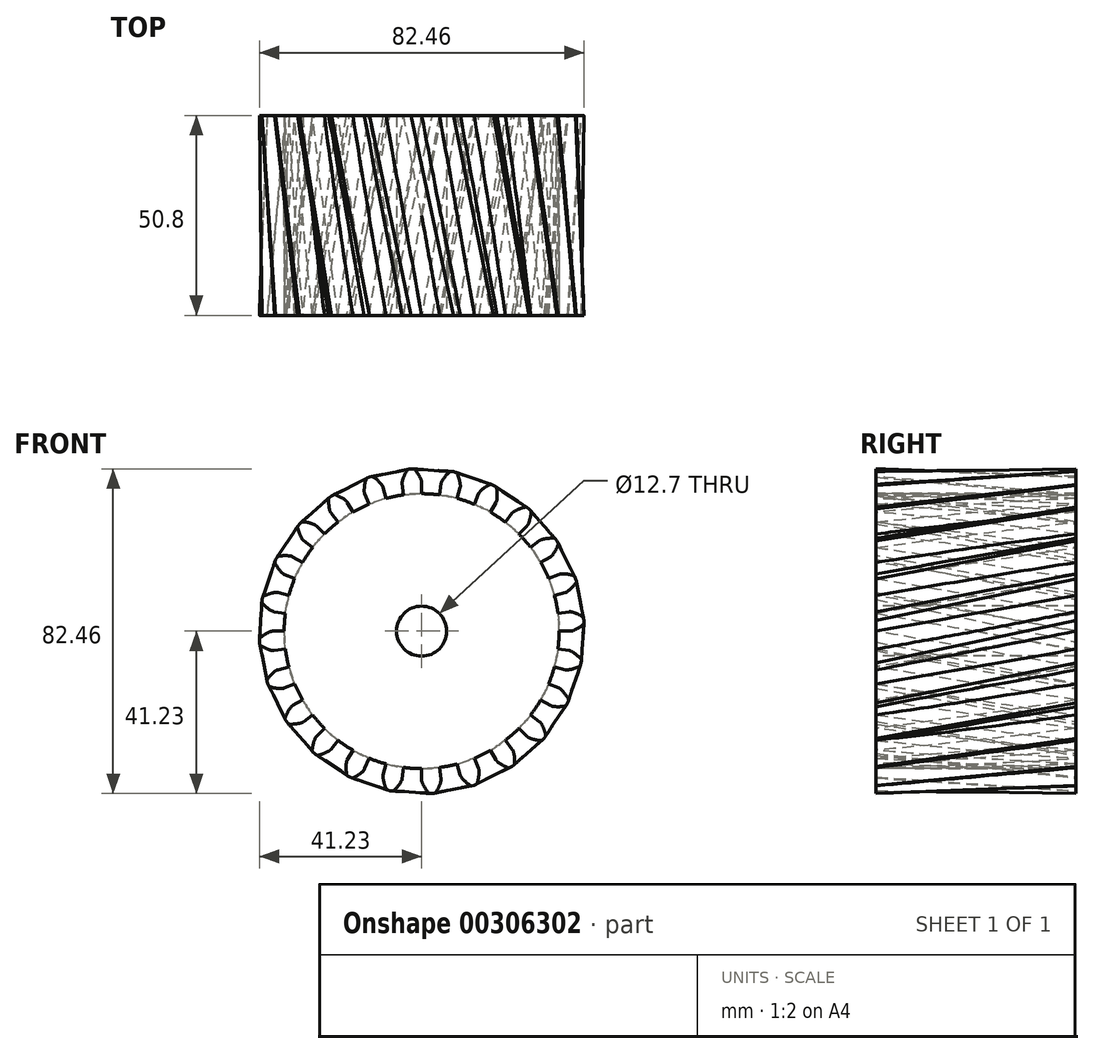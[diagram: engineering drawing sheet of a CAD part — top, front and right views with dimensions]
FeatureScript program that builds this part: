
annotation { "Feature Type Name" : "Feature", "Feature Type Description" : "" }
export const myFeature = defineFeature(function(context is Context, id is Id, definition is map)
    precondition{}
    {
        {
            var Q0;
            Q0=qCreatedBy(makeId("Front.planeOp"),FACE);
            var sketch = newSketch(context, id + "F0", { "sketchPlane" : qUnion([Q0])});
            skCircle(sketch, "E0", {"center": v(0, 0) * mm, "radius": 34.93 * mm});
            skArc(sketch, "E1.trimOffspring", {"start": v(-0.11, 38.4) * mm, "mid": v(-0.81, 39.8) * mm, "end": v(-1.73, 41.06) * mm});
            skLineSegment(sketch, "E2", {"start": v(0, 37.8) * mm, "end": v(0, 34.93) * mm});
            skLineSegment(sketch, "E3", {"start": v(-2.12, 41.23) * mm, "end": v(-2.7, 41.23) * mm});
            skArc(sketch, "E4.MirrorCS", {"start": v(-4.9, 38.09) * mm, "mid": v(-4.39, 39.56) * mm, "end": v(-3.64, 40.93) * mm});
            skLineSegment(sketch, "E5.MirrorCS", {"start": v(-4.93, 37.48) * mm, "end": v(-4.56, 34.63) * mm});
            skLineSegment(sketch, "E6.MirrorCS", {"start": v(-3.28, 41.16) * mm, "end": v(-2.7, 41.23) * mm});
            skPoint(sketch, "E7.visualSharp", {"position": v(-3.51, 41.13) * mm});
            skArc(sketch, "E7.filletArc", {"start": v(-3.28, 41.16) * mm, "mid": v(-3.49, 41.08) * mm, "end": v(-3.64, 40.93) * mm});
            skPoint(sketch, "E8.visualSharp", {"position": v(-1.89, 41.23) * mm});
            skArc(sketch, "E8.filletArc", {"start": v(-1.73, 41.06) * mm, "mid": v(-1.9, 41.19) * mm, "end": v(-2.12, 41.23) * mm});
            skPoint(sketch, "E9.visualSharp", {"position": v(0, 38.1) * mm});
            skArc(sketch, "E9.filletArc", {"start": v(0, 37.8) * mm, "mid": v(-0.03, 38.1) * mm, "end": v(-0.11, 38.4) * mm});
            skPoint(sketch, "E10.visualSharp", {"position": v(-4.97, 37.77) * mm});
            skArc(sketch, "E10.filletArc", {"start": v(-4.9, 38.09) * mm, "mid": v(-4.95, 37.79) * mm, "end": v(-4.93, 37.48) * mm});
            skSolve(sketch);
        }
        {
            var Q0;
            {var subQ0=sQuery(id+"F0.wireOp",EDGE,"E0");var subQ1=makeQuery(id+"F0.imprint","INTERSECT",VERTEX,{"derivedFrom":[subQ0,sQuery(id+"F0.wireOp",EDGE,"E2")]});Q0=makeQuery(id+"F0.imprint","IMPRINT",FACE,{"disambiguationData":[TD([[makeQuery(id+"F0.imprint","IMPRINT",EDGE,{"disambiguationData":[TD([[subQ1,-1.0]])],"derivedFrom":subQ0}),1.0]])]});}
            cPlane(context, id + "F1", {"entities" : qUnion([Q0]), "cplaneType" : CPlaneType.OFFSET, "offset" : 50.8 * mm, "width" : 152.4 * mm, "height" : 152.4 * mm});
        }
        {
            var Q0;
            Q0=qCreatedBy(id+"F1.planeOp",FACE);
            var sketch = newSketch(context, id + "F2", { "sketchPlane" : qUnion([Q0])});
            skCircle(sketch, "E11.0", {"center": v(0, 0) * mm, "radius": 34.93 * mm});
            skArc(sketch, "E12.0.0", {"start": v(-3.64, 40.93) * mm, "mid": v(-4.39, 39.56) * mm, "end": v(-4.9, 38.09) * mm});
            skArc(sketch, "E12.0.1", {"start": v(-4.9, 38.09) * mm, "mid": v(-4.95, 37.79) * mm, "end": v(-4.93, 37.48) * mm});
            skLineSegment(sketch, "E12.0.2", {"start": v(-4.93, 37.48) * mm, "end": v(-4.56, 34.63) * mm});
            skArc(sketch, "E12.0.3", {"start": v(-4.56, 34.63) * mm, "mid": v(-2.28, 34.85) * mm, "end": v(0, 34.92) * mm});
            skLineSegment(sketch, "E12.0.4", {"start": v(0, 34.93) * mm, "end": v(0, 37.8) * mm});
            skArc(sketch, "E12.0.5", {"start": v(0, 37.8) * mm, "mid": v(-0.03, 38.1) * mm, "end": v(-0.11, 38.4) * mm});
            skArc(sketch, "E12.0.6", {"start": v(-0.11, 38.4) * mm, "mid": v(-0.81, 39.8) * mm, "end": v(-1.73, 41.06) * mm});
            skArc(sketch, "E12.0.7", {"start": v(-1.73, 41.06) * mm, "mid": v(-1.9, 41.19) * mm, "end": v(-2.12, 41.23) * mm});
            skLineSegment(sketch, "E12.0.8", {"start": v(-2.12, 41.23) * mm, "end": v(-2.7, 41.23) * mm});
            skLineSegment(sketch, "E12.0.9", {"start": v(-2.7, 41.23) * mm, "end": v(-3.28, 41.16) * mm});
            skArc(sketch, "E12.0.10", {"start": v(-3.28, 41.16) * mm, "mid": v(-3.49, 41.08) * mm, "end": v(-3.64, 40.93) * mm});
            skLineSegment(sketch, "E13.1.0", {"start": v(-9.04, 33.73) * mm, "end": v(-9.79, 36.52) * mm});
            skArc(sketch, "E13.1.1", {"start": v(-9.79, 36.52) * mm, "mid": v(-9.9, 36.8) * mm, "end": v(-10.05, 37.06) * mm});
            skArc(sketch, "E13.1.2", {"start": v(-10.05, 37.06) * mm, "mid": v(-11.09, 38.23) * mm, "end": v(-12.3, 39.2) * mm});
            skArc(sketch, "E13.1.3", {"start": v(-12.3, 39.2) * mm, "mid": v(-12.5, 39.29) * mm, "end": v(-12.72, 39.28) * mm});
            skLineSegment(sketch, "E13.1.4", {"start": v(-12.72, 39.28) * mm, "end": v(-13.28, 39.13) * mm});
            skLineSegment(sketch, "E13.1.5", {"start": v(-13.28, 39.13) * mm, "end": v(-13.82, 38.9) * mm});
            skArc(sketch, "E13.1.6", {"start": v(-13.82, 38.9) * mm, "mid": v(-14, 38.78) * mm, "end": v(-14.11, 38.6) * mm});
            skArc(sketch, "E13.1.7", {"start": v(-14.11, 38.6) * mm, "mid": v(-14.48, 37.08) * mm, "end": v(-14.59, 35.52) * mm});
            skArc(sketch, "E13.1.8", {"start": v(-14.59, 35.52) * mm, "mid": v(-14.56, 35.22) * mm, "end": v(-14.47, 34.93) * mm});
            skLineSegment(sketch, "E13.1.9", {"start": v(-14.47, 34.93) * mm, "end": v(-13.37, 32.27) * mm});
            skLineSegment(sketch, "E13.2.0", {"start": v(-17.46, 30.25) * mm, "end": v(-18.9, 32.74) * mm});
            skArc(sketch, "E13.2.1", {"start": v(-18.9, 32.74) * mm, "mid": v(-19.08, 32.99) * mm, "end": v(-19.3, 33.2) * mm});
            skArc(sketch, "E13.2.2", {"start": v(-19.3, 33.2) * mm, "mid": v(-20.6, 34.06) * mm, "end": v(-22.03, 34.69) * mm});
            skArc(sketch, "E13.2.3", {"start": v(-22.03, 34.69) * mm, "mid": v(-22.24, 34.72) * mm, "end": v(-22.45, 34.65) * mm});
            skLineSegment(sketch, "E13.2.4", {"start": v(-22.45, 34.65) * mm, "end": v(-22.96, 34.36) * mm});
            skLineSegment(sketch, "E13.2.5", {"start": v(-22.96, 34.36) * mm, "end": v(-23.42, 34) * mm});
            skArc(sketch, "E13.2.6", {"start": v(-23.42, 34) * mm, "mid": v(-23.56, 33.83) * mm, "end": v(-23.62, 33.62) * mm});
            skArc(sketch, "E13.2.7", {"start": v(-23.62, 33.62) * mm, "mid": v(-23.58, 32.07) * mm, "end": v(-23.29, 30.53) * mm});
            skArc(sketch, "E13.2.8", {"start": v(-23.29, 30.53) * mm, "mid": v(-23.18, 30.25) * mm, "end": v(-23.02, 30) * mm});
            skLineSegment(sketch, "E13.2.9", {"start": v(-23.02, 30) * mm, "end": v(-21.26, 27.7) * mm});
            skLineSegment(sketch, "E13.3.0", {"start": v(-24.7, 24.7) * mm, "end": v(-26.73, 26.73) * mm});
            skArc(sketch, "E13.3.1", {"start": v(-26.73, 26.73) * mm, "mid": v(-26.97, 26.93) * mm, "end": v(-27.23, 27.07) * mm});
            skArc(sketch, "E13.3.2", {"start": v(-27.23, 27.07) * mm, "mid": v(-28.71, 27.56) * mm, "end": v(-30.25, 27.8) * mm});
            skArc(sketch, "E13.3.3", {"start": v(-30.25, 27.8) * mm, "mid": v(-30.47, 27.78) * mm, "end": v(-30.65, 27.66) * mm});
            skLineSegment(sketch, "E13.3.4", {"start": v(-30.65, 27.66) * mm, "end": v(-31.07, 27.24) * mm});
            skLineSegment(sketch, "E13.3.5", {"start": v(-31.07, 27.24) * mm, "end": v(-31.42, 26.78) * mm});
            skArc(sketch, "E13.3.6", {"start": v(-31.42, 26.78) * mm, "mid": v(-31.52, 26.58) * mm, "end": v(-31.52, 26.37) * mm});
            skArc(sketch, "E13.3.7", {"start": v(-31.52, 26.37) * mm, "mid": v(-31.08, 24.87) * mm, "end": v(-30.4, 23.47) * mm});
            skArc(sketch, "E13.3.8", {"start": v(-30.4, 23.47) * mm, "mid": v(-30.22, 23.22) * mm, "end": v(-30, 23.02) * mm});
            skLineSegment(sketch, "E13.3.9", {"start": v(-30, 23.02) * mm, "end": v(-27.7, 21.26) * mm});
            skLineSegment(sketch, "E13.4.0", {"start": v(-30.25, 17.46) * mm, "end": v(-32.74, 18.9) * mm});
            skArc(sketch, "E13.4.1", {"start": v(-32.74, 18.9) * mm, "mid": v(-33.02, 19.03) * mm, "end": v(-33.31, 19.1) * mm});
            skArc(sketch, "E13.4.2", {"start": v(-33.31, 19.1) * mm, "mid": v(-34.87, 19.2) * mm, "end": v(-36.42, 19.03) * mm});
            skArc(sketch, "E13.4.3", {"start": v(-36.42, 19.03) * mm, "mid": v(-36.62, 18.94) * mm, "end": v(-36.77, 18.78) * mm});
            skLineSegment(sketch, "E13.4.4", {"start": v(-36.77, 18.78) * mm, "end": v(-37.06, 18.28) * mm});
            skLineSegment(sketch, "E13.4.5", {"start": v(-37.06, 18.28) * mm, "end": v(-37.28, 17.73) * mm});
            skArc(sketch, "E13.4.6", {"start": v(-37.28, 17.73) * mm, "mid": v(-37.32, 17.52) * mm, "end": v(-37.27, 17.31) * mm});
            skArc(sketch, "E13.4.7", {"start": v(-37.27, 17.31) * mm, "mid": v(-36.45, 15.98) * mm, "end": v(-35.43, 14.8) * mm});
            skArc(sketch, "E13.4.8", {"start": v(-35.43, 14.8) * mm, "mid": v(-35.2, 14.61) * mm, "end": v(-34.93, 14.47) * mm});
            skLineSegment(sketch, "E13.4.9", {"start": v(-34.93, 14.47) * mm, "end": v(-32.27, 13.37) * mm});
            skLineSegment(sketch, "E13.5.0", {"start": v(-33.73, 9.04) * mm, "end": v(-36.52, 9.79) * mm});
            skArc(sketch, "E13.5.1", {"start": v(-36.52, 9.79) * mm, "mid": v(-36.82, 9.84) * mm, "end": v(-37.12, 9.83) * mm});
            skArc(sketch, "E13.5.2", {"start": v(-37.12, 9.83) * mm, "mid": v(-38.65, 9.51) * mm, "end": v(-40.1, 8.95) * mm});
            skArc(sketch, "E13.5.3", {"start": v(-40.1, 8.95) * mm, "mid": v(-40.28, 8.82) * mm, "end": v(-40.37, 8.63) * mm});
            skLineSegment(sketch, "E13.5.4", {"start": v(-40.37, 8.63) * mm, "end": v(-40.53, 8.06) * mm});
            skLineSegment(sketch, "E13.5.5", {"start": v(-40.53, 8.06) * mm, "end": v(-40.6, 7.48) * mm});
            skArc(sketch, "E13.5.6", {"start": v(-40.6, 7.48) * mm, "mid": v(-40.58, 7.26) * mm, "end": v(-40.48, 7.07) * mm});
            skArc(sketch, "E13.5.7", {"start": v(-40.48, 7.07) * mm, "mid": v(-39.35, 6) * mm, "end": v(-38.06, 5.13) * mm});
            skArc(sketch, "E13.5.8", {"start": v(-38.06, 5.13) * mm, "mid": v(-37.78, 5) * mm, "end": v(-37.48, 4.93) * mm});
            skLineSegment(sketch, "E13.5.9", {"start": v(-37.48, 4.93) * mm, "end": v(-34.63, 4.56) * mm});
            skLineSegment(sketch, "E13.6.0", {"start": v(-34.93, 0) * mm, "end": v(-37.8, 0) * mm});
            skArc(sketch, "E13.6.1", {"start": v(-37.8, 0) * mm, "mid": v(-38.1, -0.03) * mm, "end": v(-38.4, -0.11) * mm});
            skArc(sketch, "E13.6.2", {"start": v(-38.4, -0.11) * mm, "mid": v(-39.8, -0.81) * mm, "end": v(-41.06, -1.73) * mm});
            skArc(sketch, "E13.6.3", {"start": v(-41.06, -1.73) * mm, "mid": v(-41.19, -1.9) * mm, "end": v(-41.23, -2.12) * mm});
            skLineSegment(sketch, "E13.6.4", {"start": v(-41.23, -2.12) * mm, "end": v(-41.23, -2.7) * mm});
            skLineSegment(sketch, "E13.6.5", {"start": v(-41.23, -2.7) * mm, "end": v(-41.16, -3.28) * mm});
            skArc(sketch, "E13.6.6", {"start": v(-41.16, -3.28) * mm, "mid": v(-41.08, -3.49) * mm, "end": v(-40.93, -3.64) * mm});
            skArc(sketch, "E13.6.7", {"start": v(-40.93, -3.64) * mm, "mid": v(-39.56, -4.39) * mm, "end": v(-38.09, -4.9) * mm});
            skArc(sketch, "E13.6.8", {"start": v(-38.09, -4.9) * mm, "mid": v(-37.79, -4.95) * mm, "end": v(-37.48, -4.93) * mm});
            skLineSegment(sketch, "E13.6.9", {"start": v(-37.48, -4.93) * mm, "end": v(-34.63, -4.56) * mm});
            skLineSegment(sketch, "E13.7.0", {"start": v(-33.73, -9.04) * mm, "end": v(-36.52, -9.79) * mm});
            skArc(sketch, "E13.7.1", {"start": v(-36.52, -9.79) * mm, "mid": v(-36.8, -9.9) * mm, "end": v(-37.06, -10.05) * mm});
            skArc(sketch, "E13.7.2", {"start": v(-37.06, -10.05) * mm, "mid": v(-38.23, -11.09) * mm, "end": v(-39.2, -12.3) * mm});
            skArc(sketch, "E13.7.3", {"start": v(-39.2, -12.3) * mm, "mid": v(-39.29, -12.5) * mm, "end": v(-39.28, -12.72) * mm});
            skLineSegment(sketch, "E13.7.4", {"start": v(-39.28, -12.72) * mm, "end": v(-39.13, -13.28) * mm});
            skLineSegment(sketch, "E13.7.5", {"start": v(-39.13, -13.28) * mm, "end": v(-38.9, -13.82) * mm});
            skArc(sketch, "E13.7.6", {"start": v(-38.9, -13.82) * mm, "mid": v(-38.78, -14) * mm, "end": v(-38.6, -14.11) * mm});
            skArc(sketch, "E13.7.7", {"start": v(-38.6, -14.11) * mm, "mid": v(-37.08, -14.48) * mm, "end": v(-35.52, -14.59) * mm});
            skArc(sketch, "E13.7.8", {"start": v(-35.52, -14.59) * mm, "mid": v(-35.22, -14.56) * mm, "end": v(-34.93, -14.47) * mm});
            skLineSegment(sketch, "E13.7.9", {"start": v(-34.93, -14.47) * mm, "end": v(-32.27, -13.37) * mm});
            skLineSegment(sketch, "E13.8.0", {"start": v(-30.25, -17.46) * mm, "end": v(-32.74, -18.9) * mm});
            skArc(sketch, "E13.8.1", {"start": v(-32.74, -18.9) * mm, "mid": v(-32.99, -19.08) * mm, "end": v(-33.2, -19.3) * mm});
            skArc(sketch, "E13.8.2", {"start": v(-33.2, -19.3) * mm, "mid": v(-34.06, -20.6) * mm, "end": v(-34.69, -22.03) * mm});
            skArc(sketch, "E13.8.3", {"start": v(-34.69, -22.03) * mm, "mid": v(-34.72, -22.24) * mm, "end": v(-34.65, -22.45) * mm});
            skLineSegment(sketch, "E13.8.4", {"start": v(-34.65, -22.45) * mm, "end": v(-34.36, -22.96) * mm});
            skLineSegment(sketch, "E13.8.5", {"start": v(-34.36, -22.96) * mm, "end": v(-34, -23.42) * mm});
            skArc(sketch, "E13.8.6", {"start": v(-34, -23.42) * mm, "mid": v(-33.83, -23.56) * mm, "end": v(-33.62, -23.62) * mm});
            skArc(sketch, "E13.8.7", {"start": v(-33.62, -23.62) * mm, "mid": v(-32.07, -23.58) * mm, "end": v(-30.53, -23.29) * mm});
            skArc(sketch, "E13.8.8", {"start": v(-30.53, -23.29) * mm, "mid": v(-30.25, -23.18) * mm, "end": v(-30, -23.02) * mm});
            skLineSegment(sketch, "E13.8.9", {"start": v(-30, -23.02) * mm, "end": v(-27.7, -21.26) * mm});
            skLineSegment(sketch, "E13.9.0", {"start": v(-24.7, -24.7) * mm, "end": v(-26.73, -26.73) * mm});
            skArc(sketch, "E13.9.1", {"start": v(-26.73, -26.73) * mm, "mid": v(-26.93, -26.97) * mm, "end": v(-27.07, -27.23) * mm});
            skArc(sketch, "E13.9.2", {"start": v(-27.07, -27.23) * mm, "mid": v(-27.56, -28.71) * mm, "end": v(-27.8, -30.25) * mm});
            skArc(sketch, "E13.9.3", {"start": v(-27.8, -30.25) * mm, "mid": v(-27.78, -30.47) * mm, "end": v(-27.66, -30.65) * mm});
            skLineSegment(sketch, "E13.9.4", {"start": v(-27.66, -30.65) * mm, "end": v(-27.24, -31.07) * mm});
            skLineSegment(sketch, "E13.9.5", {"start": v(-27.24, -31.07) * mm, "end": v(-26.78, -31.42) * mm});
            skArc(sketch, "E13.9.6", {"start": v(-26.78, -31.42) * mm, "mid": v(-26.58, -31.52) * mm, "end": v(-26.37, -31.52) * mm});
            skArc(sketch, "E13.9.7", {"start": v(-26.37, -31.52) * mm, "mid": v(-24.87, -31.08) * mm, "end": v(-23.47, -30.4) * mm});
            skArc(sketch, "E13.9.8", {"start": v(-23.47, -30.4) * mm, "mid": v(-23.22, -30.22) * mm, "end": v(-23.02, -30) * mm});
            skLineSegment(sketch, "E13.9.9", {"start": v(-23.02, -30) * mm, "end": v(-21.26, -27.7) * mm});
            skLineSegment(sketch, "E13.10.0", {"start": v(-17.46, -30.25) * mm, "end": v(-18.9, -32.74) * mm});
            skArc(sketch, "E13.10.1", {"start": v(-18.9, -32.74) * mm, "mid": v(-19.03, -33.02) * mm, "end": v(-19.1, -33.31) * mm});
            skArc(sketch, "E13.10.2", {"start": v(-19.1, -33.31) * mm, "mid": v(-19.2, -34.87) * mm, "end": v(-19.03, -36.42) * mm});
            skArc(sketch, "E13.10.3", {"start": v(-19.03, -36.42) * mm, "mid": v(-18.94, -36.62) * mm, "end": v(-18.78, -36.77) * mm});
            skLineSegment(sketch, "E13.10.4", {"start": v(-18.78, -36.77) * mm, "end": v(-18.28, -37.06) * mm});
            skLineSegment(sketch, "E13.10.5", {"start": v(-18.28, -37.06) * mm, "end": v(-17.73, -37.28) * mm});
            skArc(sketch, "E13.10.6", {"start": v(-17.73, -37.28) * mm, "mid": v(-17.52, -37.32) * mm, "end": v(-17.31, -37.27) * mm});
            skArc(sketch, "E13.10.7", {"start": v(-17.31, -37.27) * mm, "mid": v(-15.98, -36.45) * mm, "end": v(-14.8, -35.43) * mm});
            skArc(sketch, "E13.10.8", {"start": v(-14.8, -35.43) * mm, "mid": v(-14.61, -35.2) * mm, "end": v(-14.47, -34.93) * mm});
            skLineSegment(sketch, "E13.10.9", {"start": v(-14.47, -34.93) * mm, "end": v(-13.37, -32.27) * mm});
            skLineSegment(sketch, "E13.11.0", {"start": v(-9.04, -33.73) * mm, "end": v(-9.79, -36.52) * mm});
            skArc(sketch, "E13.11.1", {"start": v(-9.79, -36.52) * mm, "mid": v(-9.84, -36.82) * mm, "end": v(-9.83, -37.12) * mm});
            skArc(sketch, "E13.11.2", {"start": v(-9.83, -37.12) * mm, "mid": v(-9.51, -38.65) * mm, "end": v(-8.95, -40.1) * mm});
            skArc(sketch, "E13.11.3", {"start": v(-8.95, -40.1) * mm, "mid": v(-8.82, -40.28) * mm, "end": v(-8.63, -40.37) * mm});
            skLineSegment(sketch, "E13.11.4", {"start": v(-8.63, -40.37) * mm, "end": v(-8.06, -40.53) * mm});
            skLineSegment(sketch, "E13.11.5", {"start": v(-8.06, -40.53) * mm, "end": v(-7.48, -40.6) * mm});
            skArc(sketch, "E13.11.6", {"start": v(-7.48, -40.6) * mm, "mid": v(-7.26, -40.58) * mm, "end": v(-7.07, -40.48) * mm});
            skArc(sketch, "E13.11.7", {"start": v(-7.07, -40.48) * mm, "mid": v(-6, -39.35) * mm, "end": v(-5.13, -38.06) * mm});
            skArc(sketch, "E13.11.8", {"start": v(-5.13, -38.06) * mm, "mid": v(-5, -37.78) * mm, "end": v(-4.93, -37.48) * mm});
            skLineSegment(sketch, "E13.11.9", {"start": v(-4.93, -37.48) * mm, "end": v(-4.56, -34.63) * mm});
            skLineSegment(sketch, "E13.12.0", {"start": v(0, -34.93) * mm, "end": v(0, -37.8) * mm});
            skArc(sketch, "E13.12.1", {"start": v(0, -37.8) * mm, "mid": v(0.03, -38.1) * mm, "end": v(0.11, -38.4) * mm});
            skArc(sketch, "E13.12.2", {"start": v(0.11, -38.4) * mm, "mid": v(0.81, -39.8) * mm, "end": v(1.73, -41.06) * mm});
            skArc(sketch, "E13.12.3", {"start": v(1.73, -41.06) * mm, "mid": v(1.9, -41.19) * mm, "end": v(2.12, -41.23) * mm});
            skLineSegment(sketch, "E13.12.4", {"start": v(2.12, -41.23) * mm, "end": v(2.7, -41.23) * mm});
            skLineSegment(sketch, "E13.12.5", {"start": v(2.7, -41.23) * mm, "end": v(3.28, -41.16) * mm});
            skArc(sketch, "E13.12.6", {"start": v(3.28, -41.16) * mm, "mid": v(3.49, -41.08) * mm, "end": v(3.64, -40.93) * mm});
            skArc(sketch, "E13.12.7", {"start": v(3.64, -40.93) * mm, "mid": v(4.39, -39.56) * mm, "end": v(4.9, -38.09) * mm});
            skArc(sketch, "E13.12.8", {"start": v(4.9, -38.09) * mm, "mid": v(4.95, -37.79) * mm, "end": v(4.93, -37.48) * mm});
            skLineSegment(sketch, "E13.12.9", {"start": v(4.93, -37.48) * mm, "end": v(4.56, -34.63) * mm});
            skLineSegment(sketch, "E13.13.0", {"start": v(9.04, -33.73) * mm, "end": v(9.79, -36.52) * mm});
            skArc(sketch, "E13.13.1", {"start": v(9.79, -36.52) * mm, "mid": v(9.9, -36.8) * mm, "end": v(10.05, -37.06) * mm});
            skArc(sketch, "E13.13.2", {"start": v(10.05, -37.06) * mm, "mid": v(11.09, -38.23) * mm, "end": v(12.3, -39.2) * mm});
            skArc(sketch, "E13.13.3", {"start": v(12.3, -39.2) * mm, "mid": v(12.5, -39.29) * mm, "end": v(12.72, -39.28) * mm});
            skLineSegment(sketch, "E13.13.4", {"start": v(12.72, -39.28) * mm, "end": v(13.28, -39.13) * mm});
            skLineSegment(sketch, "E13.13.5", {"start": v(13.28, -39.13) * mm, "end": v(13.82, -38.9) * mm});
            skArc(sketch, "E13.13.6", {"start": v(13.82, -38.9) * mm, "mid": v(14, -38.78) * mm, "end": v(14.11, -38.6) * mm});
            skArc(sketch, "E13.13.7", {"start": v(14.11, -38.6) * mm, "mid": v(14.48, -37.08) * mm, "end": v(14.59, -35.52) * mm});
            skArc(sketch, "E13.13.8", {"start": v(14.59, -35.52) * mm, "mid": v(14.56, -35.22) * mm, "end": v(14.47, -34.93) * mm});
            skLineSegment(sketch, "E13.13.9", {"start": v(14.47, -34.93) * mm, "end": v(13.37, -32.27) * mm});
            skLineSegment(sketch, "E13.14.0", {"start": v(17.46, -30.25) * mm, "end": v(18.9, -32.74) * mm});
            skArc(sketch, "E13.14.1", {"start": v(18.9, -32.74) * mm, "mid": v(19.08, -32.99) * mm, "end": v(19.3, -33.2) * mm});
            skArc(sketch, "E13.14.2", {"start": v(19.3, -33.2) * mm, "mid": v(20.6, -34.06) * mm, "end": v(22.03, -34.69) * mm});
            skArc(sketch, "E13.14.3", {"start": v(22.03, -34.69) * mm, "mid": v(22.24, -34.72) * mm, "end": v(22.45, -34.65) * mm});
            skLineSegment(sketch, "E13.14.4", {"start": v(22.45, -34.65) * mm, "end": v(22.96, -34.36) * mm});
            skLineSegment(sketch, "E13.14.5", {"start": v(22.96, -34.36) * mm, "end": v(23.42, -34) * mm});
            skArc(sketch, "E13.14.6", {"start": v(23.42, -34) * mm, "mid": v(23.56, -33.83) * mm, "end": v(23.62, -33.62) * mm});
            skArc(sketch, "E13.14.7", {"start": v(23.62, -33.62) * mm, "mid": v(23.58, -32.07) * mm, "end": v(23.29, -30.53) * mm});
            skArc(sketch, "E13.14.8", {"start": v(23.29, -30.53) * mm, "mid": v(23.18, -30.25) * mm, "end": v(23.02, -30) * mm});
            skLineSegment(sketch, "E13.14.9", {"start": v(23.02, -30) * mm, "end": v(21.26, -27.7) * mm});
            skLineSegment(sketch, "E13.15.0", {"start": v(24.7, -24.7) * mm, "end": v(26.73, -26.73) * mm});
            skArc(sketch, "E13.15.1", {"start": v(26.73, -26.73) * mm, "mid": v(26.97, -26.93) * mm, "end": v(27.23, -27.07) * mm});
            skArc(sketch, "E13.15.2", {"start": v(27.23, -27.07) * mm, "mid": v(28.71, -27.56) * mm, "end": v(30.25, -27.8) * mm});
            skArc(sketch, "E13.15.3", {"start": v(30.25, -27.8) * mm, "mid": v(30.47, -27.78) * mm, "end": v(30.65, -27.66) * mm});
            skLineSegment(sketch, "E13.15.4", {"start": v(30.65, -27.66) * mm, "end": v(31.07, -27.24) * mm});
            skLineSegment(sketch, "E13.15.5", {"start": v(31.07, -27.24) * mm, "end": v(31.42, -26.78) * mm});
            skArc(sketch, "E13.15.6", {"start": v(31.42, -26.78) * mm, "mid": v(31.52, -26.58) * mm, "end": v(31.52, -26.37) * mm});
            skArc(sketch, "E13.15.7", {"start": v(31.52, -26.37) * mm, "mid": v(31.08, -24.87) * mm, "end": v(30.4, -23.47) * mm});
            skArc(sketch, "E13.15.8", {"start": v(30.4, -23.47) * mm, "mid": v(30.22, -23.22) * mm, "end": v(30, -23.02) * mm});
            skLineSegment(sketch, "E13.15.9", {"start": v(30, -23.02) * mm, "end": v(27.7, -21.26) * mm});
            skLineSegment(sketch, "E13.16.0", {"start": v(30.25, -17.46) * mm, "end": v(32.74, -18.9) * mm});
            skArc(sketch, "E13.16.1", {"start": v(32.74, -18.9) * mm, "mid": v(33.02, -19.03) * mm, "end": v(33.31, -19.1) * mm});
            skArc(sketch, "E13.16.2", {"start": v(33.31, -19.1) * mm, "mid": v(34.87, -19.2) * mm, "end": v(36.42, -19.03) * mm});
            skArc(sketch, "E13.16.3", {"start": v(36.42, -19.03) * mm, "mid": v(36.62, -18.94) * mm, "end": v(36.77, -18.78) * mm});
            skLineSegment(sketch, "E13.16.4", {"start": v(36.77, -18.78) * mm, "end": v(37.06, -18.28) * mm});
            skLineSegment(sketch, "E13.16.5", {"start": v(37.06, -18.28) * mm, "end": v(37.28, -17.73) * mm});
            skArc(sketch, "E13.16.6", {"start": v(37.28, -17.73) * mm, "mid": v(37.32, -17.52) * mm, "end": v(37.27, -17.31) * mm});
            skArc(sketch, "E13.16.7", {"start": v(37.27, -17.31) * mm, "mid": v(36.45, -15.98) * mm, "end": v(35.43, -14.8) * mm});
            skArc(sketch, "E13.16.8", {"start": v(35.43, -14.8) * mm, "mid": v(35.2, -14.61) * mm, "end": v(34.93, -14.47) * mm});
            skLineSegment(sketch, "E13.16.9", {"start": v(34.93, -14.47) * mm, "end": v(32.27, -13.37) * mm});
            skLineSegment(sketch, "E13.17.0", {"start": v(33.73, -9.04) * mm, "end": v(36.52, -9.79) * mm});
            skArc(sketch, "E13.17.1", {"start": v(36.52, -9.79) * mm, "mid": v(36.82, -9.84) * mm, "end": v(37.12, -9.83) * mm});
            skArc(sketch, "E13.17.2", {"start": v(37.12, -9.83) * mm, "mid": v(38.65, -9.51) * mm, "end": v(40.1, -8.95) * mm});
            skArc(sketch, "E13.17.3", {"start": v(40.1, -8.95) * mm, "mid": v(40.28, -8.82) * mm, "end": v(40.37, -8.63) * mm});
            skLineSegment(sketch, "E13.17.4", {"start": v(40.37, -8.63) * mm, "end": v(40.53, -8.06) * mm});
            skLineSegment(sketch, "E13.17.5", {"start": v(40.53, -8.06) * mm, "end": v(40.6, -7.48) * mm});
            skArc(sketch, "E13.17.6", {"start": v(40.6, -7.48) * mm, "mid": v(40.58, -7.26) * mm, "end": v(40.48, -7.07) * mm});
            skArc(sketch, "E13.17.7", {"start": v(40.48, -7.07) * mm, "mid": v(39.35, -6) * mm, "end": v(38.06, -5.13) * mm});
            skArc(sketch, "E13.17.8", {"start": v(38.06, -5.13) * mm, "mid": v(37.78, -5) * mm, "end": v(37.48, -4.93) * mm});
            skLineSegment(sketch, "E13.17.9", {"start": v(37.48, -4.93) * mm, "end": v(34.63, -4.56) * mm});
            skLineSegment(sketch, "E13.18.0", {"start": v(34.93, 0) * mm, "end": v(37.8, 0) * mm});
            skArc(sketch, "E13.18.1", {"start": v(37.8, 0) * mm, "mid": v(38.1, 0.03) * mm, "end": v(38.4, 0.11) * mm});
            skArc(sketch, "E13.18.2", {"start": v(38.4, 0.11) * mm, "mid": v(39.8, 0.81) * mm, "end": v(41.06, 1.73) * mm});
            skArc(sketch, "E13.18.3", {"start": v(41.06, 1.73) * mm, "mid": v(41.19, 1.9) * mm, "end": v(41.23, 2.12) * mm});
            skLineSegment(sketch, "E13.18.4", {"start": v(41.23, 2.12) * mm, "end": v(41.23, 2.7) * mm});
            skLineSegment(sketch, "E13.18.5", {"start": v(41.23, 2.7) * mm, "end": v(41.16, 3.28) * mm});
            skArc(sketch, "E13.18.6", {"start": v(41.16, 3.28) * mm, "mid": v(41.08, 3.49) * mm, "end": v(40.93, 3.64) * mm});
            skArc(sketch, "E13.18.7", {"start": v(40.93, 3.64) * mm, "mid": v(39.56, 4.39) * mm, "end": v(38.09, 4.9) * mm});
            skArc(sketch, "E13.18.8", {"start": v(38.09, 4.9) * mm, "mid": v(37.79, 4.95) * mm, "end": v(37.48, 4.93) * mm});
            skLineSegment(sketch, "E13.18.9", {"start": v(37.48, 4.93) * mm, "end": v(34.63, 4.56) * mm});
            skLineSegment(sketch, "E13.19.0", {"start": v(33.73, 9.04) * mm, "end": v(36.52, 9.79) * mm});
            skArc(sketch, "E13.19.1", {"start": v(36.52, 9.79) * mm, "mid": v(36.8, 9.9) * mm, "end": v(37.06, 10.05) * mm});
            skArc(sketch, "E13.19.2", {"start": v(37.06, 10.05) * mm, "mid": v(38.23, 11.09) * mm, "end": v(39.2, 12.3) * mm});
            skArc(sketch, "E13.19.3", {"start": v(39.2, 12.3) * mm, "mid": v(39.29, 12.5) * mm, "end": v(39.28, 12.72) * mm});
            skLineSegment(sketch, "E13.19.4", {"start": v(39.28, 12.72) * mm, "end": v(39.13, 13.28) * mm});
            skLineSegment(sketch, "E13.19.5", {"start": v(39.13, 13.28) * mm, "end": v(38.9, 13.82) * mm});
            skArc(sketch, "E13.19.6", {"start": v(38.9, 13.82) * mm, "mid": v(38.78, 14) * mm, "end": v(38.6, 14.11) * mm});
            skArc(sketch, "E13.19.7", {"start": v(38.6, 14.11) * mm, "mid": v(37.08, 14.48) * mm, "end": v(35.52, 14.59) * mm});
            skArc(sketch, "E13.19.8", {"start": v(35.52, 14.59) * mm, "mid": v(35.22, 14.56) * mm, "end": v(34.93, 14.47) * mm});
            skLineSegment(sketch, "E13.19.9", {"start": v(34.93, 14.47) * mm, "end": v(32.27, 13.37) * mm});
            skLineSegment(sketch, "E13.20.0", {"start": v(30.25, 17.46) * mm, "end": v(32.74, 18.9) * mm});
            skArc(sketch, "E13.20.1", {"start": v(32.74, 18.9) * mm, "mid": v(32.99, 19.08) * mm, "end": v(33.2, 19.3) * mm});
            skArc(sketch, "E13.20.2", {"start": v(33.2, 19.3) * mm, "mid": v(34.06, 20.6) * mm, "end": v(34.69, 22.03) * mm});
            skArc(sketch, "E13.20.3", {"start": v(34.69, 22.03) * mm, "mid": v(34.72, 22.24) * mm, "end": v(34.65, 22.45) * mm});
            skLineSegment(sketch, "E13.20.4", {"start": v(34.65, 22.45) * mm, "end": v(34.36, 22.96) * mm});
            skLineSegment(sketch, "E13.20.5", {"start": v(34.36, 22.96) * mm, "end": v(34, 23.42) * mm});
            skArc(sketch, "E13.20.6", {"start": v(34, 23.42) * mm, "mid": v(33.83, 23.56) * mm, "end": v(33.62, 23.62) * mm});
            skArc(sketch, "E13.20.7", {"start": v(33.62, 23.62) * mm, "mid": v(32.07, 23.58) * mm, "end": v(30.53, 23.29) * mm});
            skArc(sketch, "E13.20.8", {"start": v(30.53, 23.29) * mm, "mid": v(30.25, 23.18) * mm, "end": v(30, 23.02) * mm});
            skLineSegment(sketch, "E13.20.9", {"start": v(30, 23.02) * mm, "end": v(27.7, 21.26) * mm});
            skLineSegment(sketch, "E13.21.0", {"start": v(24.7, 24.7) * mm, "end": v(26.73, 26.73) * mm});
            skArc(sketch, "E13.21.1", {"start": v(26.73, 26.73) * mm, "mid": v(26.93, 26.97) * mm, "end": v(27.07, 27.23) * mm});
            skArc(sketch, "E13.21.2", {"start": v(27.07, 27.23) * mm, "mid": v(27.56, 28.71) * mm, "end": v(27.8, 30.25) * mm});
            skArc(sketch, "E13.21.3", {"start": v(27.8, 30.25) * mm, "mid": v(27.78, 30.47) * mm, "end": v(27.66, 30.65) * mm});
            skLineSegment(sketch, "E13.21.4", {"start": v(27.66, 30.65) * mm, "end": v(27.24, 31.07) * mm});
            skLineSegment(sketch, "E13.21.5", {"start": v(27.24, 31.07) * mm, "end": v(26.78, 31.42) * mm});
            skArc(sketch, "E13.21.6", {"start": v(26.78, 31.42) * mm, "mid": v(26.58, 31.52) * mm, "end": v(26.37, 31.52) * mm});
            skArc(sketch, "E13.21.7", {"start": v(26.37, 31.52) * mm, "mid": v(24.87, 31.08) * mm, "end": v(23.47, 30.4) * mm});
            skArc(sketch, "E13.21.8", {"start": v(23.47, 30.4) * mm, "mid": v(23.22, 30.22) * mm, "end": v(23.02, 30) * mm});
            skLineSegment(sketch, "E13.21.9", {"start": v(23.02, 30) * mm, "end": v(21.26, 27.7) * mm});
            skLineSegment(sketch, "E13.22.0", {"start": v(17.46, 30.25) * mm, "end": v(18.9, 32.74) * mm});
            skArc(sketch, "E13.22.1", {"start": v(18.9, 32.74) * mm, "mid": v(19.03, 33.02) * mm, "end": v(19.1, 33.31) * mm});
            skArc(sketch, "E13.22.2", {"start": v(19.1, 33.31) * mm, "mid": v(19.2, 34.87) * mm, "end": v(19.03, 36.42) * mm});
            skArc(sketch, "E13.22.3", {"start": v(19.03, 36.42) * mm, "mid": v(18.94, 36.62) * mm, "end": v(18.78, 36.77) * mm});
            skLineSegment(sketch, "E13.22.4", {"start": v(18.78, 36.77) * mm, "end": v(18.28, 37.06) * mm});
            skLineSegment(sketch, "E13.22.5", {"start": v(18.28, 37.06) * mm, "end": v(17.73, 37.28) * mm});
            skArc(sketch, "E13.22.6", {"start": v(17.73, 37.28) * mm, "mid": v(17.52, 37.32) * mm, "end": v(17.31, 37.27) * mm});
            skArc(sketch, "E13.22.7", {"start": v(17.31, 37.27) * mm, "mid": v(15.98, 36.45) * mm, "end": v(14.8, 35.43) * mm});
            skArc(sketch, "E13.22.8", {"start": v(14.8, 35.43) * mm, "mid": v(14.61, 35.2) * mm, "end": v(14.47, 34.93) * mm});
            skLineSegment(sketch, "E13.22.9", {"start": v(14.47, 34.93) * mm, "end": v(13.37, 32.27) * mm});
            skLineSegment(sketch, "E13.23.0", {"start": v(9.04, 33.73) * mm, "end": v(9.79, 36.52) * mm});
            skArc(sketch, "E13.23.1", {"start": v(9.79, 36.52) * mm, "mid": v(9.84, 36.82) * mm, "end": v(9.83, 37.12) * mm});
            skArc(sketch, "E13.23.2", {"start": v(9.83, 37.12) * mm, "mid": v(9.51, 38.65) * mm, "end": v(8.95, 40.1) * mm});
            skArc(sketch, "E13.23.3", {"start": v(8.95, 40.1) * mm, "mid": v(8.82, 40.28) * mm, "end": v(8.63, 40.37) * mm});
            skLineSegment(sketch, "E13.23.4", {"start": v(8.63, 40.37) * mm, "end": v(8.06, 40.53) * mm});
            skLineSegment(sketch, "E13.23.5", {"start": v(8.06, 40.53) * mm, "end": v(7.48, 40.6) * mm});
            skArc(sketch, "E13.23.6", {"start": v(7.48, 40.6) * mm, "mid": v(7.26, 40.58) * mm, "end": v(7.07, 40.48) * mm});
            skArc(sketch, "E13.23.7", {"start": v(7.07, 40.48) * mm, "mid": v(6, 39.35) * mm, "end": v(5.13, 38.06) * mm});
            skArc(sketch, "E13.23.8", {"start": v(5.13, 38.06) * mm, "mid": v(5, 37.78) * mm, "end": v(4.93, 37.48) * mm});
            skLineSegment(sketch, "E13.23.9", {"start": v(4.93, 37.48) * mm, "end": v(4.56, 34.63) * mm});
            skSolve(sketch);
        }
        {
            var Q0;
            {var subQ0=sQuery(id+"F2.wireOp",EDGE,"E13.23.0");Q0=makeQuery(id+"F2.imprint","IMPRINT",FACE,{"disambiguationData":[TD([[makeQuery(id+"F2.imprint","IMPRINT",EDGE,{"derivedFrom":subQ0}),1.0]])]});}
            var Q1;
            Q1=makeQuery(id+"F0.imprint","IMPRINT",FACE,{"disambiguationData":[TD([[makeQuery(id+"F0.imprint","IMPRINT",EDGE,{"derivedFrom":sQuery(id+"F0.wireOp",EDGE,"E1.trimOffspring")}),1.0]])]});
            loft(context, id + "F3", {"sheetProfilesArray" : [{ "sheetProfileEntities" : qUnion([Q0]) }, { "sheetProfileEntities" : qUnion([Q1]) }]});
        }
        {
            var Q0;
            Q0=qCreatedBy(id+"F1.planeOp",FACE);
            var sketch = newSketch(context, id + "F4", { "sketchPlane" : qUnion([Q0])});
            skCircle(sketch, "E14", {"center": v(0, 0) * mm, "radius": 34.93 * mm});
            skSolve(sketch);
        }
        {
            var Q0;
            Q0=makeQuery(id+"F4.imprint","IMPRINT",FACE,{"disambiguationData":[TD([[makeQuery(id+"F4.imprint","IMPRINT",EDGE,{"derivedFrom":sQuery(id+"F4.wireOp",EDGE,"E14")}),1.0]])]});
            var Q1;
            Q1=makeQuery(id+"F3.opLoft","CAP_FACE",FACE,{"disambiguationData":[OSD([makeQuery(id+"F0.imprint","IMPRINT",FACE,{"disambiguationData":[TD([[makeQuery(id+"F0.imprint","IMPRINT",EDGE,{"derivedFrom":sQuery(id+"F0.wireOp",EDGE,"E1.trimOffspring")}),1.0]])]})])],"isStart":true});
            extrude(context, id + "F5", {"entities" : qUnion([Q0]), "operationType" : NewBodyOperationType.ADD, "endBound" : BoundingType.UP_TO_SURFACE, "oppositeDirection" : true, "endBoundEntityFace" : qUnion([Q1]), "depth" : 25.4 * mm});
        }
        {
            var Q0;
            {var subQ0=sQuery(id+"F2.wireOp",EDGE,"E13.23.0");Q0=makeQuery(id+"F3.opLoft","SWEPT_BODY",BODY,{"disambiguationData":[OSD([makeQuery(id+"F0.imprint","IMPRINT",FACE,{"disambiguationData":[TD([[makeQuery(id+"F0.imprint","IMPRINT",EDGE,{"derivedFrom":sQuery(id+"F0.wireOp",EDGE,"E1.trimOffspring")}),1.0]])]}),makeQuery(id+"F2.imprint","IMPRINT",FACE,{"disambiguationData":[TD([[makeQuery(id+"F2.imprint","IMPRINT",EDGE,{"derivedFrom":subQ0}),1.0]])]})])]});}
            var Q1;
            Q1=makeQuery(id+"F5.opExtrude","SWEPT_FACE",FACE,{"disambiguationData":[OSD([sQuery(id+"F4.wireOp",EDGE,"E14")])]});
            circularPattern(context, id + "F6", {"entities" : qUnion([Q0]), "axis" : qUnion([Q1]), "angle" : 360 * degree, "instanceCount" : 24, "equalSpace" : true});
        }
        {
            var Q0;
            {var subQ0=sQuery(id+"F2.wireOp",EDGE,"E13.23.0");Q0=makeQuery(id+"F6.opPattern","COPY",BODY,{"derivedFrom":makeQuery(id+"F3.opLoft","SWEPT_BODY",BODY,{"disambiguationData":[OSD([makeQuery(id+"F0.imprint","IMPRINT",FACE,{"disambiguationData":[TD([[makeQuery(id+"F0.imprint","IMPRINT",EDGE,{"derivedFrom":sQuery(id+"F0.wireOp",EDGE,"E1.trimOffspring")}),1.0]])]}),makeQuery(id+"F2.imprint","IMPRINT",FACE,{"disambiguationData":[TD([[makeQuery(id+"F2.imprint","IMPRINT",EDGE,{"derivedFrom":subQ0}),1.0]])]})])]}),"instanceName":"5"});}
            var Q1;
            {var subQ0=sQuery(id+"F2.wireOp",EDGE,"E13.23.0");Q1=makeQuery(id+"F3.opLoft","SWEPT_BODY",BODY,{"disambiguationData":[OSD([makeQuery(id+"F0.imprint","IMPRINT",FACE,{"disambiguationData":[TD([[makeQuery(id+"F0.imprint","IMPRINT",EDGE,{"derivedFrom":sQuery(id+"F0.wireOp",EDGE,"E1.trimOffspring")}),1.0]])]}),makeQuery(id+"F2.imprint","IMPRINT",FACE,{"disambiguationData":[TD([[makeQuery(id+"F2.imprint","IMPRINT",EDGE,{"derivedFrom":subQ0}),1.0]])]})])]});}
            var Q2;
            {var subQ0=sQuery(id+"F2.wireOp",EDGE,"E13.23.0");Q2=makeQuery(id+"F6.opPattern","COPY",BODY,{"derivedFrom":makeQuery(id+"F3.opLoft","SWEPT_BODY",BODY,{"disambiguationData":[OSD([makeQuery(id+"F0.imprint","IMPRINT",FACE,{"disambiguationData":[TD([[makeQuery(id+"F0.imprint","IMPRINT",EDGE,{"derivedFrom":sQuery(id+"F0.wireOp",EDGE,"E1.trimOffspring")}),1.0]])]}),makeQuery(id+"F2.imprint","IMPRINT",FACE,{"disambiguationData":[TD([[makeQuery(id+"F2.imprint","IMPRINT",EDGE,{"derivedFrom":subQ0}),1.0]])]})])]}),"instanceName":"23"});}
            var Q3;
            {var subQ0=sQuery(id+"F2.wireOp",EDGE,"E13.23.0");Q3=makeQuery(id+"F6.opPattern","COPY",BODY,{"derivedFrom":makeQuery(id+"F3.opLoft","SWEPT_BODY",BODY,{"disambiguationData":[OSD([makeQuery(id+"F0.imprint","IMPRINT",FACE,{"disambiguationData":[TD([[makeQuery(id+"F0.imprint","IMPRINT",EDGE,{"derivedFrom":sQuery(id+"F0.wireOp",EDGE,"E1.trimOffspring")}),1.0]])]}),makeQuery(id+"F2.imprint","IMPRINT",FACE,{"disambiguationData":[TD([[makeQuery(id+"F2.imprint","IMPRINT",EDGE,{"derivedFrom":subQ0}),1.0]])]})])]}),"instanceName":"22"});}
            var Q4;
            {var subQ0=sQuery(id+"F2.wireOp",EDGE,"E13.23.0");Q4=makeQuery(id+"F6.opPattern","COPY",BODY,{"derivedFrom":makeQuery(id+"F3.opLoft","SWEPT_BODY",BODY,{"disambiguationData":[OSD([makeQuery(id+"F0.imprint","IMPRINT",FACE,{"disambiguationData":[TD([[makeQuery(id+"F0.imprint","IMPRINT",EDGE,{"derivedFrom":sQuery(id+"F0.wireOp",EDGE,"E1.trimOffspring")}),1.0]])]}),makeQuery(id+"F2.imprint","IMPRINT",FACE,{"disambiguationData":[TD([[makeQuery(id+"F2.imprint","IMPRINT",EDGE,{"derivedFrom":subQ0}),1.0]])]})])]}),"instanceName":"21"});}
            var Q5;
            {var subQ0=sQuery(id+"F2.wireOp",EDGE,"E13.23.0");Q5=makeQuery(id+"F6.opPattern","COPY",BODY,{"derivedFrom":makeQuery(id+"F3.opLoft","SWEPT_BODY",BODY,{"disambiguationData":[OSD([makeQuery(id+"F0.imprint","IMPRINT",FACE,{"disambiguationData":[TD([[makeQuery(id+"F0.imprint","IMPRINT",EDGE,{"derivedFrom":sQuery(id+"F0.wireOp",EDGE,"E1.trimOffspring")}),1.0]])]}),makeQuery(id+"F2.imprint","IMPRINT",FACE,{"disambiguationData":[TD([[makeQuery(id+"F2.imprint","IMPRINT",EDGE,{"derivedFrom":subQ0}),1.0]])]})])]}),"instanceName":"20"});}
            var Q6;
            {var subQ0=sQuery(id+"F2.wireOp",EDGE,"E13.23.0");Q6=makeQuery(id+"F6.opPattern","COPY",BODY,{"derivedFrom":makeQuery(id+"F3.opLoft","SWEPT_BODY",BODY,{"disambiguationData":[OSD([makeQuery(id+"F0.imprint","IMPRINT",FACE,{"disambiguationData":[TD([[makeQuery(id+"F0.imprint","IMPRINT",EDGE,{"derivedFrom":sQuery(id+"F0.wireOp",EDGE,"E1.trimOffspring")}),1.0]])]}),makeQuery(id+"F2.imprint","IMPRINT",FACE,{"disambiguationData":[TD([[makeQuery(id+"F2.imprint","IMPRINT",EDGE,{"derivedFrom":subQ0}),1.0]])]})])]}),"instanceName":"19"});}
            var Q7;
            {var subQ0=sQuery(id+"F2.wireOp",EDGE,"E13.23.0");Q7=makeQuery(id+"F6.opPattern","COPY",BODY,{"derivedFrom":makeQuery(id+"F3.opLoft","SWEPT_BODY",BODY,{"disambiguationData":[OSD([makeQuery(id+"F0.imprint","IMPRINT",FACE,{"disambiguationData":[TD([[makeQuery(id+"F0.imprint","IMPRINT",EDGE,{"derivedFrom":sQuery(id+"F0.wireOp",EDGE,"E1.trimOffspring")}),1.0]])]}),makeQuery(id+"F2.imprint","IMPRINT",FACE,{"disambiguationData":[TD([[makeQuery(id+"F2.imprint","IMPRINT",EDGE,{"derivedFrom":subQ0}),1.0]])]})])]}),"instanceName":"18"});}
            var Q8;
            {var subQ0=sQuery(id+"F2.wireOp",EDGE,"E13.23.0");Q8=makeQuery(id+"F6.opPattern","COPY",BODY,{"derivedFrom":makeQuery(id+"F3.opLoft","SWEPT_BODY",BODY,{"disambiguationData":[OSD([makeQuery(id+"F0.imprint","IMPRINT",FACE,{"disambiguationData":[TD([[makeQuery(id+"F0.imprint","IMPRINT",EDGE,{"derivedFrom":sQuery(id+"F0.wireOp",EDGE,"E1.trimOffspring")}),1.0]])]}),makeQuery(id+"F2.imprint","IMPRINT",FACE,{"disambiguationData":[TD([[makeQuery(id+"F2.imprint","IMPRINT",EDGE,{"derivedFrom":subQ0}),1.0]])]})])]}),"instanceName":"17"});}
            var Q9;
            {var subQ0=sQuery(id+"F2.wireOp",EDGE,"E13.23.0");Q9=makeQuery(id+"F6.opPattern","COPY",BODY,{"derivedFrom":makeQuery(id+"F3.opLoft","SWEPT_BODY",BODY,{"disambiguationData":[OSD([makeQuery(id+"F0.imprint","IMPRINT",FACE,{"disambiguationData":[TD([[makeQuery(id+"F0.imprint","IMPRINT",EDGE,{"derivedFrom":sQuery(id+"F0.wireOp",EDGE,"E1.trimOffspring")}),1.0]])]}),makeQuery(id+"F2.imprint","IMPRINT",FACE,{"disambiguationData":[TD([[makeQuery(id+"F2.imprint","IMPRINT",EDGE,{"derivedFrom":subQ0}),1.0]])]})])]}),"instanceName":"16"});}
            var Q10;
            {var subQ0=sQuery(id+"F2.wireOp",EDGE,"E13.23.0");Q10=makeQuery(id+"F6.opPattern","COPY",BODY,{"derivedFrom":makeQuery(id+"F3.opLoft","SWEPT_BODY",BODY,{"disambiguationData":[OSD([makeQuery(id+"F0.imprint","IMPRINT",FACE,{"disambiguationData":[TD([[makeQuery(id+"F0.imprint","IMPRINT",EDGE,{"derivedFrom":sQuery(id+"F0.wireOp",EDGE,"E1.trimOffspring")}),1.0]])]}),makeQuery(id+"F2.imprint","IMPRINT",FACE,{"disambiguationData":[TD([[makeQuery(id+"F2.imprint","IMPRINT",EDGE,{"derivedFrom":subQ0}),1.0]])]})])]}),"instanceName":"15"});}
            var Q11;
            {var subQ0=sQuery(id+"F2.wireOp",EDGE,"E13.23.0");Q11=makeQuery(id+"F6.opPattern","COPY",BODY,{"derivedFrom":makeQuery(id+"F3.opLoft","SWEPT_BODY",BODY,{"disambiguationData":[OSD([makeQuery(id+"F0.imprint","IMPRINT",FACE,{"disambiguationData":[TD([[makeQuery(id+"F0.imprint","IMPRINT",EDGE,{"derivedFrom":sQuery(id+"F0.wireOp",EDGE,"E1.trimOffspring")}),1.0]])]}),makeQuery(id+"F2.imprint","IMPRINT",FACE,{"disambiguationData":[TD([[makeQuery(id+"F2.imprint","IMPRINT",EDGE,{"derivedFrom":subQ0}),1.0]])]})])]}),"instanceName":"14"});}
            var Q12;
            {var subQ0=sQuery(id+"F2.wireOp",EDGE,"E13.23.0");Q12=makeQuery(id+"F6.opPattern","COPY",BODY,{"derivedFrom":makeQuery(id+"F3.opLoft","SWEPT_BODY",BODY,{"disambiguationData":[OSD([makeQuery(id+"F0.imprint","IMPRINT",FACE,{"disambiguationData":[TD([[makeQuery(id+"F0.imprint","IMPRINT",EDGE,{"derivedFrom":sQuery(id+"F0.wireOp",EDGE,"E1.trimOffspring")}),1.0]])]}),makeQuery(id+"F2.imprint","IMPRINT",FACE,{"disambiguationData":[TD([[makeQuery(id+"F2.imprint","IMPRINT",EDGE,{"derivedFrom":subQ0}),1.0]])]})])]}),"instanceName":"13"});}
            var Q13;
            {var subQ0=sQuery(id+"F2.wireOp",EDGE,"E13.23.0");Q13=makeQuery(id+"F6.opPattern","COPY",BODY,{"derivedFrom":makeQuery(id+"F3.opLoft","SWEPT_BODY",BODY,{"disambiguationData":[OSD([makeQuery(id+"F0.imprint","IMPRINT",FACE,{"disambiguationData":[TD([[makeQuery(id+"F0.imprint","IMPRINT",EDGE,{"derivedFrom":sQuery(id+"F0.wireOp",EDGE,"E1.trimOffspring")}),1.0]])]}),makeQuery(id+"F2.imprint","IMPRINT",FACE,{"disambiguationData":[TD([[makeQuery(id+"F2.imprint","IMPRINT",EDGE,{"derivedFrom":subQ0}),1.0]])]})])]}),"instanceName":"12"});}
            var Q14;
            {var subQ0=sQuery(id+"F2.wireOp",EDGE,"E13.23.0");Q14=makeQuery(id+"F6.opPattern","COPY",BODY,{"derivedFrom":makeQuery(id+"F3.opLoft","SWEPT_BODY",BODY,{"disambiguationData":[OSD([makeQuery(id+"F0.imprint","IMPRINT",FACE,{"disambiguationData":[TD([[makeQuery(id+"F0.imprint","IMPRINT",EDGE,{"derivedFrom":sQuery(id+"F0.wireOp",EDGE,"E1.trimOffspring")}),1.0]])]}),makeQuery(id+"F2.imprint","IMPRINT",FACE,{"disambiguationData":[TD([[makeQuery(id+"F2.imprint","IMPRINT",EDGE,{"derivedFrom":subQ0}),1.0]])]})])]}),"instanceName":"11"});}
            var Q15;
            {var subQ0=sQuery(id+"F2.wireOp",EDGE,"E13.23.0");Q15=makeQuery(id+"F6.opPattern","COPY",BODY,{"derivedFrom":makeQuery(id+"F3.opLoft","SWEPT_BODY",BODY,{"disambiguationData":[OSD([makeQuery(id+"F0.imprint","IMPRINT",FACE,{"disambiguationData":[TD([[makeQuery(id+"F0.imprint","IMPRINT",EDGE,{"derivedFrom":sQuery(id+"F0.wireOp",EDGE,"E1.trimOffspring")}),1.0]])]}),makeQuery(id+"F2.imprint","IMPRINT",FACE,{"disambiguationData":[TD([[makeQuery(id+"F2.imprint","IMPRINT",EDGE,{"derivedFrom":subQ0}),1.0]])]})])]}),"instanceName":"10"});}
            var Q16;
            {var subQ0=sQuery(id+"F2.wireOp",EDGE,"E13.23.0");Q16=makeQuery(id+"F6.opPattern","COPY",BODY,{"derivedFrom":makeQuery(id+"F3.opLoft","SWEPT_BODY",BODY,{"disambiguationData":[OSD([makeQuery(id+"F0.imprint","IMPRINT",FACE,{"disambiguationData":[TD([[makeQuery(id+"F0.imprint","IMPRINT",EDGE,{"derivedFrom":sQuery(id+"F0.wireOp",EDGE,"E1.trimOffspring")}),1.0]])]}),makeQuery(id+"F2.imprint","IMPRINT",FACE,{"disambiguationData":[TD([[makeQuery(id+"F2.imprint","IMPRINT",EDGE,{"derivedFrom":subQ0}),1.0]])]})])]}),"instanceName":"9"});}
            var Q17;
            {var subQ0=sQuery(id+"F2.wireOp",EDGE,"E13.23.0");Q17=makeQuery(id+"F6.opPattern","COPY",BODY,{"derivedFrom":makeQuery(id+"F3.opLoft","SWEPT_BODY",BODY,{"disambiguationData":[OSD([makeQuery(id+"F0.imprint","IMPRINT",FACE,{"disambiguationData":[TD([[makeQuery(id+"F0.imprint","IMPRINT",EDGE,{"derivedFrom":sQuery(id+"F0.wireOp",EDGE,"E1.trimOffspring")}),1.0]])]}),makeQuery(id+"F2.imprint","IMPRINT",FACE,{"disambiguationData":[TD([[makeQuery(id+"F2.imprint","IMPRINT",EDGE,{"derivedFrom":subQ0}),1.0]])]})])]}),"instanceName":"8"});}
            var Q18;
            {var subQ0=sQuery(id+"F2.wireOp",EDGE,"E13.23.0");Q18=makeQuery(id+"F6.opPattern","COPY",BODY,{"derivedFrom":makeQuery(id+"F3.opLoft","SWEPT_BODY",BODY,{"disambiguationData":[OSD([makeQuery(id+"F0.imprint","IMPRINT",FACE,{"disambiguationData":[TD([[makeQuery(id+"F0.imprint","IMPRINT",EDGE,{"derivedFrom":sQuery(id+"F0.wireOp",EDGE,"E1.trimOffspring")}),1.0]])]}),makeQuery(id+"F2.imprint","IMPRINT",FACE,{"disambiguationData":[TD([[makeQuery(id+"F2.imprint","IMPRINT",EDGE,{"derivedFrom":subQ0}),1.0]])]})])]}),"instanceName":"7"});}
            var Q19;
            {var subQ0=sQuery(id+"F2.wireOp",EDGE,"E13.23.0");Q19=makeQuery(id+"F6.opPattern","COPY",BODY,{"derivedFrom":makeQuery(id+"F3.opLoft","SWEPT_BODY",BODY,{"disambiguationData":[OSD([makeQuery(id+"F0.imprint","IMPRINT",FACE,{"disambiguationData":[TD([[makeQuery(id+"F0.imprint","IMPRINT",EDGE,{"derivedFrom":sQuery(id+"F0.wireOp",EDGE,"E1.trimOffspring")}),1.0]])]}),makeQuery(id+"F2.imprint","IMPRINT",FACE,{"disambiguationData":[TD([[makeQuery(id+"F2.imprint","IMPRINT",EDGE,{"derivedFrom":subQ0}),1.0]])]})])]}),"instanceName":"6"});}
            var Q20;
            {var subQ0=sQuery(id+"F2.wireOp",EDGE,"E13.23.0");Q20=makeQuery(id+"F6.opPattern","COPY",BODY,{"derivedFrom":makeQuery(id+"F3.opLoft","SWEPT_BODY",BODY,{"disambiguationData":[OSD([makeQuery(id+"F0.imprint","IMPRINT",FACE,{"disambiguationData":[TD([[makeQuery(id+"F0.imprint","IMPRINT",EDGE,{"derivedFrom":sQuery(id+"F0.wireOp",EDGE,"E1.trimOffspring")}),1.0]])]}),makeQuery(id+"F2.imprint","IMPRINT",FACE,{"disambiguationData":[TD([[makeQuery(id+"F2.imprint","IMPRINT",EDGE,{"derivedFrom":subQ0}),1.0]])]})])]}),"instanceName":"4"});}
            var Q21;
            {var subQ0=sQuery(id+"F2.wireOp",EDGE,"E13.23.0");Q21=makeQuery(id+"F6.opPattern","COPY",BODY,{"derivedFrom":makeQuery(id+"F3.opLoft","SWEPT_BODY",BODY,{"disambiguationData":[OSD([makeQuery(id+"F0.imprint","IMPRINT",FACE,{"disambiguationData":[TD([[makeQuery(id+"F0.imprint","IMPRINT",EDGE,{"derivedFrom":sQuery(id+"F0.wireOp",EDGE,"E1.trimOffspring")}),1.0]])]}),makeQuery(id+"F2.imprint","IMPRINT",FACE,{"disambiguationData":[TD([[makeQuery(id+"F2.imprint","IMPRINT",EDGE,{"derivedFrom":subQ0}),1.0]])]})])]}),"instanceName":"3"});}
            var Q22;
            {var subQ0=sQuery(id+"F2.wireOp",EDGE,"E13.23.0");Q22=makeQuery(id+"F6.opPattern","COPY",BODY,{"derivedFrom":makeQuery(id+"F3.opLoft","SWEPT_BODY",BODY,{"disambiguationData":[OSD([makeQuery(id+"F0.imprint","IMPRINT",FACE,{"disambiguationData":[TD([[makeQuery(id+"F0.imprint","IMPRINT",EDGE,{"derivedFrom":sQuery(id+"F0.wireOp",EDGE,"E1.trimOffspring")}),1.0]])]}),makeQuery(id+"F2.imprint","IMPRINT",FACE,{"disambiguationData":[TD([[makeQuery(id+"F2.imprint","IMPRINT",EDGE,{"derivedFrom":subQ0}),1.0]])]})])]}),"instanceName":"2"});}
            var Q23;
            {var subQ0=sQuery(id+"F2.wireOp",EDGE,"E13.23.0");Q23=makeQuery(id+"F6.opPattern","COPY",BODY,{"derivedFrom":makeQuery(id+"F3.opLoft","SWEPT_BODY",BODY,{"disambiguationData":[OSD([makeQuery(id+"F0.imprint","IMPRINT",FACE,{"disambiguationData":[TD([[makeQuery(id+"F0.imprint","IMPRINT",EDGE,{"derivedFrom":sQuery(id+"F0.wireOp",EDGE,"E1.trimOffspring")}),1.0]])]}),makeQuery(id+"F2.imprint","IMPRINT",FACE,{"disambiguationData":[TD([[makeQuery(id+"F2.imprint","IMPRINT",EDGE,{"derivedFrom":subQ0}),1.0]])]})])]}),"instanceName":"1"});}
            booleanBodies(context, id + "F7", {"operationType" : BooleanOperationType.UNION, "tools" : qUnion([Q0, Q1, Q2, Q3, Q4, Q5, Q6, Q7, Q8, Q9, Q10, Q11, Q12, Q13, Q14, Q15, Q16, Q17, Q18, Q19, Q20, Q21, Q22, Q23])});
        }
        {
            var Q0;
            {var subQ0=sQuery(id+"F2.wireOp",EDGE,"E13.23.0");var subQ3=makeQuery(id+"F5.boolean.opBoolean","MERGE",FACE,{"derivedFrom":[makeQuery(id+"F3.opLoft","CAP_FACE",FACE,{"disambiguationData":[OSD([makeQuery(id+"F2.imprint","IMPRINT",FACE,{"disambiguationData":[TD([[makeQuery(id+"F2.imprint","IMPRINT",EDGE,{"derivedFrom":subQ0}),1.0]])]})])],"isStart":true}),makeQuery(id+"F5.opExtrude","CAP_FACE",FACE,{"disambiguationData":[OSD([sQuery(id+"F4.wireOp",EDGE,"E14")])],"isStart":true})]});Q0=makeQuery(id+"F7.opBoolean","MERGE",FACE,{"derivedFrom":[subQ3,makeQuery(id+"F6.opPattern","COPY",FACE,{"derivedFrom":subQ3,"instanceName":"1"}),makeQuery(id+"F6.opPattern","COPY",FACE,{"derivedFrom":subQ3,"instanceName":"2"}),makeQuery(id+"F6.opPattern","COPY",FACE,{"derivedFrom":subQ3,"instanceName":"3"}),makeQuery(id+"F6.opPattern","COPY",FACE,{"derivedFrom":subQ3,"instanceName":"4"}),makeQuery(id+"F6.opPattern","COPY",FACE,{"derivedFrom":subQ3,"instanceName":"5"}),makeQuery(id+"F6.opPattern","COPY",FACE,{"derivedFrom":subQ3,"instanceName":"6"}),makeQuery(id+"F6.opPattern","COPY",FACE,{"derivedFrom":subQ3,"instanceName":"7"}),makeQuery(id+"F6.opPattern","COPY",FACE,{"derivedFrom":subQ3,"instanceName":"8"}),makeQuery(id+"F6.opPattern","COPY",FACE,{"derivedFrom":subQ3,"instanceName":"9"}),makeQuery(id+"F6.opPattern","COPY",FACE,{"derivedFrom":subQ3,"instanceName":"10"}),makeQuery(id+"F6.opPattern","COPY",FACE,{"derivedFrom":subQ3,"instanceName":"11"}),makeQuery(id+"F6.opPattern","COPY",FACE,{"derivedFrom":subQ3,"instanceName":"12"}),makeQuery(id+"F6.opPattern","COPY",FACE,{"derivedFrom":subQ3,"instanceName":"13"}),makeQuery(id+"F6.opPattern","COPY",FACE,{"derivedFrom":subQ3,"instanceName":"14"}),makeQuery(id+"F6.opPattern","COPY",FACE,{"derivedFrom":subQ3,"instanceName":"15"}),makeQuery(id+"F6.opPattern","COPY",FACE,{"derivedFrom":subQ3,"instanceName":"16"}),makeQuery(id+"F6.opPattern","COPY",FACE,{"derivedFrom":subQ3,"instanceName":"17"}),makeQuery(id+"F6.opPattern","COPY",FACE,{"derivedFrom":subQ3,"instanceName":"18"}),makeQuery(id+"F6.opPattern","COPY",FACE,{"derivedFrom":subQ3,"instanceName":"19"}),makeQuery(id+"F6.opPattern","COPY",FACE,{"derivedFrom":subQ3,"instanceName":"20"}),makeQuery(id+"F6.opPattern","COPY",FACE,{"derivedFrom":subQ3,"instanceName":"21"}),makeQuery(id+"F6.opPattern","COPY",FACE,{"derivedFrom":subQ3,"instanceName":"22"}),makeQuery(id+"F6.opPattern","COPY",FACE,{"derivedFrom":subQ3,"instanceName":"23"})]});}
            var sketch = newSketch(context, id + "F8", { "sketchPlane" : qUnion([Q0])});
            skPoint(sketch, "E15", {"position": v(0, 0) * mm});
            skSolve(sketch);
        }
        {
            var Q0;
            Q0=sQuery(id+"F8.wireOp",VERTEX,"E15");
            var Q1;
            {var subQ0=sQuery(id+"F2.wireOp",EDGE,"E13.23.0");Q1=makeQuery(id+"F6.opPattern","COPY",BODY,{"derivedFrom":makeQuery(id+"F3.opLoft","SWEPT_BODY",BODY,{"disambiguationData":[OSD([makeQuery(id+"F0.imprint","IMPRINT",FACE,{"disambiguationData":[TD([[makeQuery(id+"F0.imprint","IMPRINT",EDGE,{"derivedFrom":sQuery(id+"F0.wireOp",EDGE,"E1.trimOffspring")}),1.0]])]}),makeQuery(id+"F2.imprint","IMPRINT",FACE,{"disambiguationData":[TD([[makeQuery(id+"F2.imprint","IMPRINT",EDGE,{"derivedFrom":subQ0}),1.0]])]})])]}),"instanceName":"5"});}
            hole(context, id + "F9", {"style" : HoleStyle.SIMPLE, "endStyle" : HoleEndStyle.THROUGH, "holeDiameter" : 12.7 * mm, "tappedDepth" : 12.7 * mm, "tapClearance" : 3, "locations" : qUnion([Q0]), "scope" : qUnion([Q1])});
        }
    });
